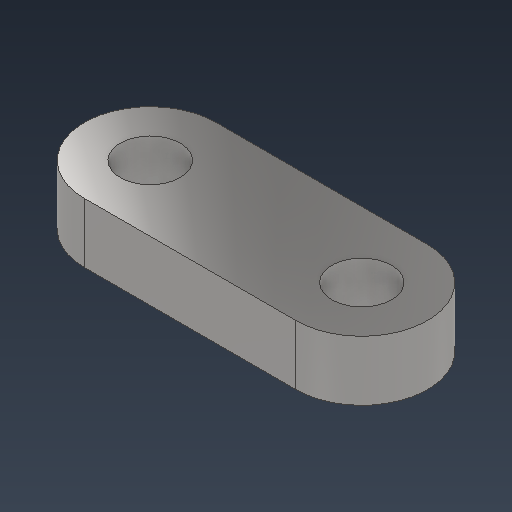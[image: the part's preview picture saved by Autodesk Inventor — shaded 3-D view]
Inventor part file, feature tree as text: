
AUTODESK INVENTOR PART (.ipt)
format: ipt  version: 2021 (Build 250183000, 183)  size: 123,392 bytes
history: native  units: mm
features: sketch x2, extrude x1, hole x1
ambient origin geometry x8: Origin, YZ Plane, XZ Plane, XY Plane, X Axis, Y Axis, Z Axis, Center Point
bodies: Solid1 (feature_tree)
feature tree (4):
  extrude  "Extrusion1"  Depth=5.5mm
  hole  "Hole1"  [1 undecoded]
  sketch  "Sketch1"  dims[d0=11.0mm d1=5.5mm]
  sketch  "Sketch2"  dims[d2=17.686mm d3=5.0mm d4=0.0mm d5=0.0mm d6=0.0mm d7=0.0mm d8=0.0mm d9=5.0mm d10=6.0mm d11=4.0mm d12=2.0mm d13=90.0deg d14=8.0mm d15=20.594885mm]
note: 1 required parameter value undecoded (feature->parameter linkage not recoverable at this tier; creation-order binding heuristic only, values carry confidence <= 0.55)
